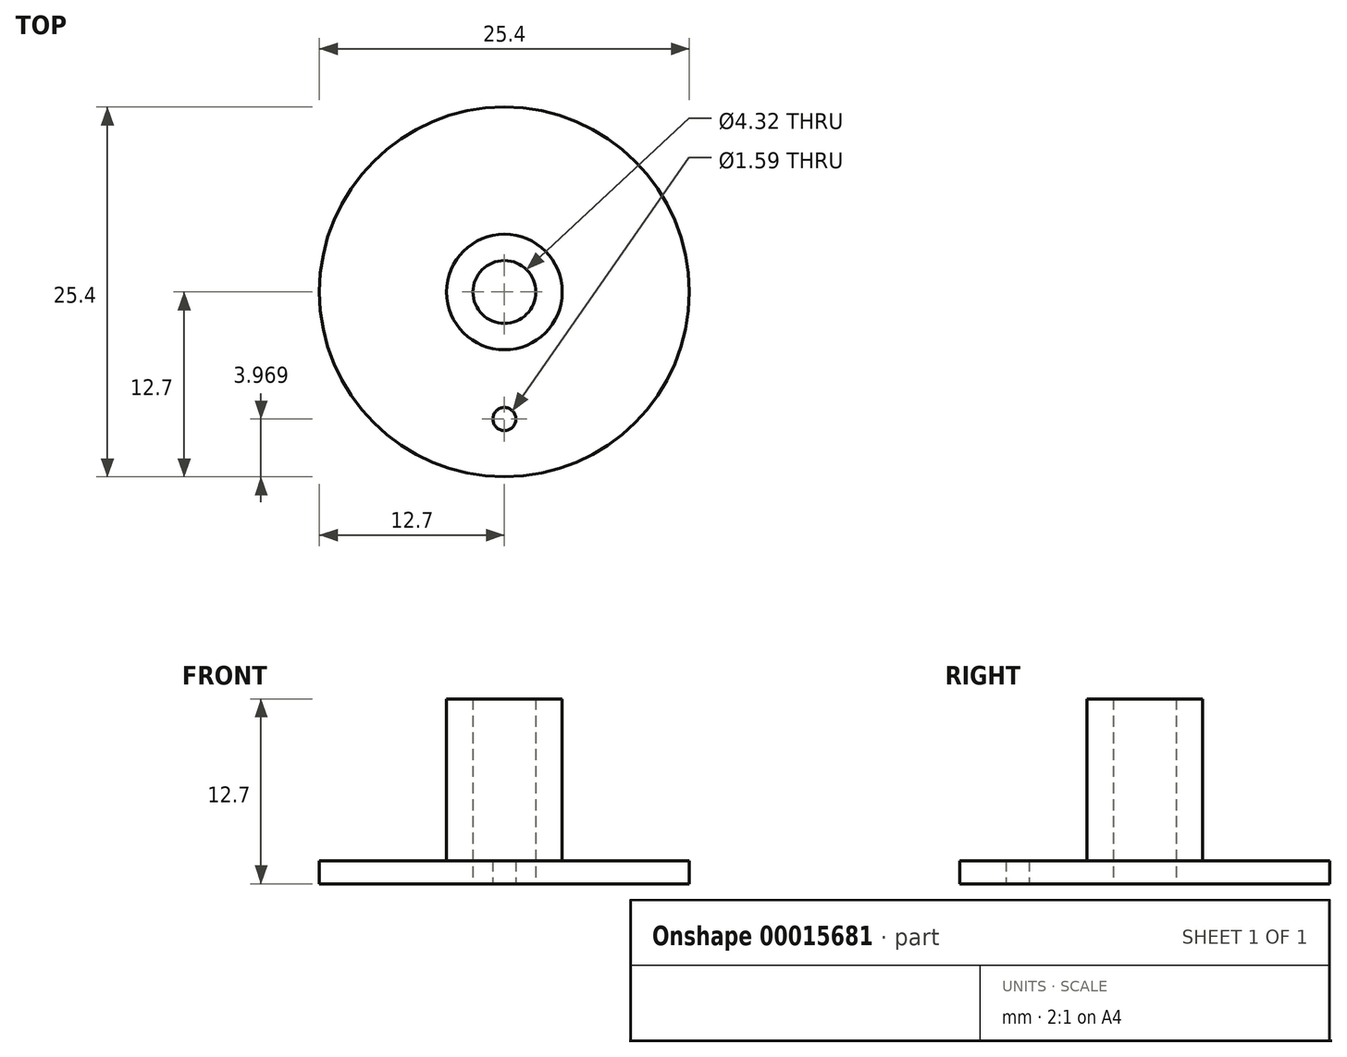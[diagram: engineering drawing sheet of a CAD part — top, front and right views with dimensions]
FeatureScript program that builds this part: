
annotation { "Feature Type Name" : "Feature", "Feature Type Description" : "" }
export const myFeature = defineFeature(function(context is Context, id is Id, definition is map)
    precondition{}
    {
        {
            var Q0;
            Q0=qCreatedBy(makeId("Top.planeOp"),FACE);
            var sketch = newSketch(context, id + "F0", { "sketchPlane" : qUnion([Q0])});
            skCircle(sketch, "E0", {"center": v(0, 0) * mm, "radius": 12.7 * mm});
            skCircle(sketch, "E1", {"center": v(0, 0) * mm, "radius": 2.16 * mm});
            skSolve(sketch);
        }
        {
            var Q0;
            Q0 = qSketchRegion(id + "F0", true);
            extrude(context, id + "F1", {"entities" : qUnion([Q0]), "depth" : 12.7 * mm});
        }
        {
            var Q0;
            Q0=makeQuery(id+"F1.opExtrude","CAP_FACE",FACE,{"disambiguationData":[OSD([sQuery(id+"F0.wireOp",EDGE,"E0"),sQuery(id+"F0.wireOp",EDGE,"E1")])],"isStart":false});
            var sketch = newSketch(context, id + "F2", { "sketchPlane" : qUnion([Q0])});
            skCircle(sketch, "E2", {"center": v(0, 0) * mm, "radius": 3.97 * mm});
            skCircle(sketch, "E3", {"center": v(0, 0) * mm, "radius": 12.7 * mm});
            skSolve(sketch);
        }
        {
            var Q0;
            Q0 = qSketchRegion(id + "F2", true);
            extrude(context, id + "F3", {"entities" : qUnion([Q0]), "operationType" : NewBodyOperationType.REMOVE, "oppositeDirection" : true, "depth" : 11.1 * mm});
        }
        {
            var Q0;
            Q0=makeQuery(id+"F1.opExtrude","CAP_FACE",FACE,{"disambiguationData":[OSD([sQuery(id+"F0.wireOp",EDGE,"E0"),sQuery(id+"F0.wireOp",EDGE,"E1")])],"isStart":true});
            var sketch = newSketch(context, id + "F4", { "sketchPlane" : qUnion([Q0])});
            skLineSegment(sketch, "E4", {"start": v(0, 0) * mm, "end": v(0, 8.73) * mm, "construction": true});
            skCircle(sketch, "E5", {"center": v(0, 8.73) * mm, "radius": 0.8 * mm});
            skCircle(sketch, "E6", {"center": v(0, 8.73) * mm, "radius": 3.97 * mm, "construction": true});
            skSolve(sketch);
        }
        {
            var Q0;
            Q0 = qSketchRegion(id + "F4", true);
            var Q1;
            Q1=makeQuery(id+"F3.boolean.opBoolean","COPY",FACE,{"derivedFrom":makeQuery(id+"F3.opExtrude","CAP_FACE",FACE,{"disambiguationData":[OSD([sQuery(id+"F2.wireOp",EDGE,"E2"),sQuery(id+"F2.wireOp",EDGE,"E3")])],"isStart":false})});
            extrude(context, id + "F5", {"entities" : qUnion([Q0]), "operationType" : NewBodyOperationType.REMOVE, "endBound" : BoundingType.UP_TO_SURFACE, "oppositeDirection" : true, "endBoundEntityFace" : qUnion([Q1]), "depth" : 25.4 * mm});
        }
    });
